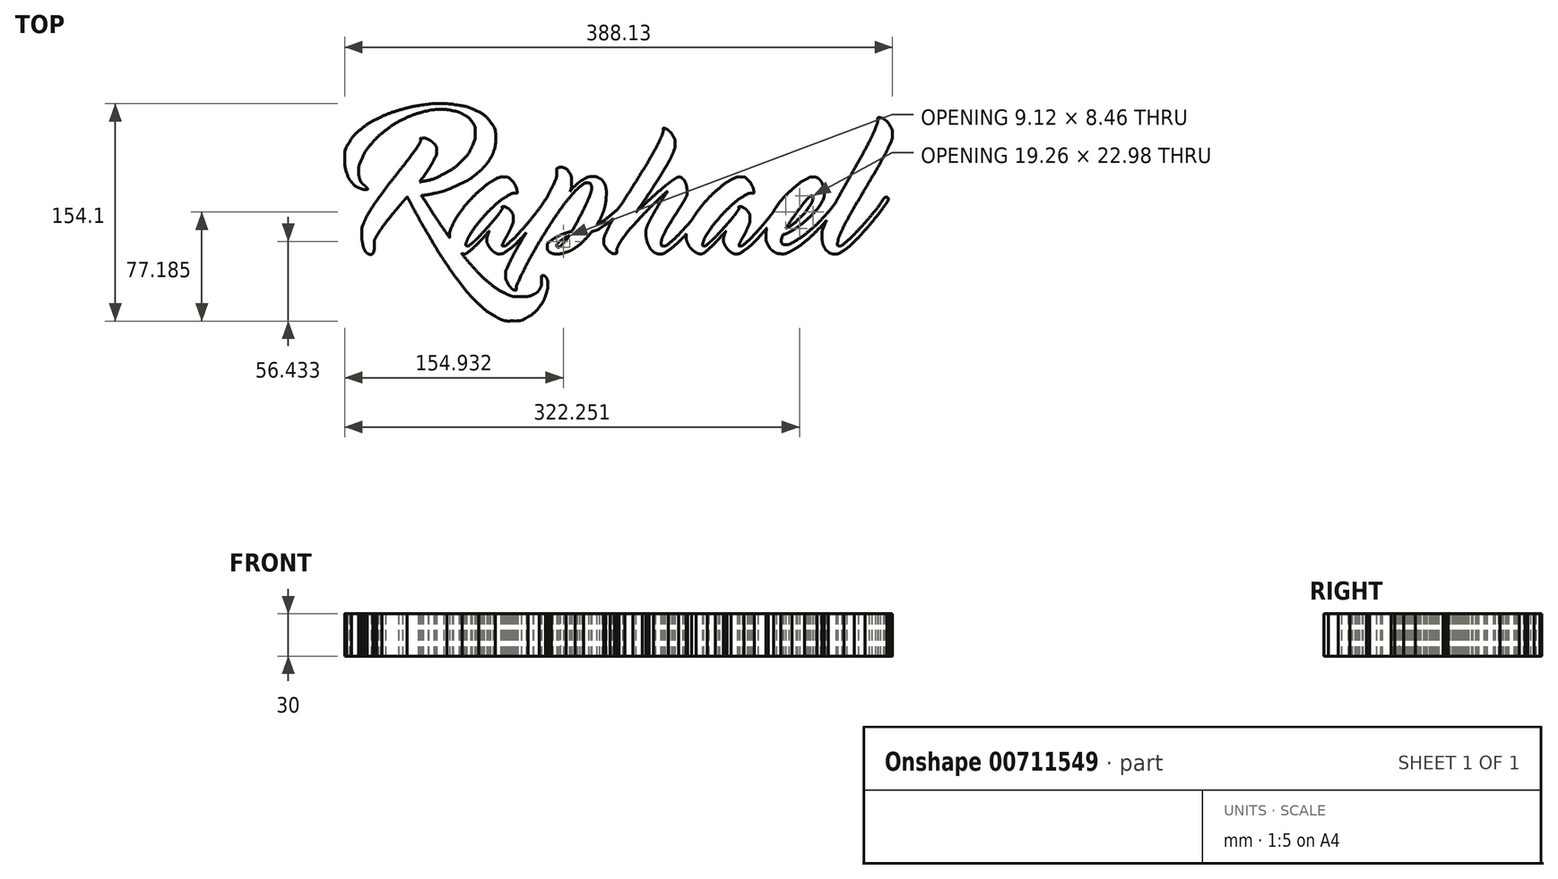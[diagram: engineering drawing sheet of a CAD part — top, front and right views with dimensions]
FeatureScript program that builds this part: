
annotation { "Feature Type Name" : "Feature", "Feature Type Description" : "" }
export const myFeature = defineFeature(function(context is Context, id is Id, definition is map)
    precondition{}
    {
        {
            var Q0;
            Q0=qCreatedBy(makeId("Top.planeOp"), FACE);
            var sketch = newSketch(context, id + "F0", { "sketchPlane" : qUnion([Q0])});
            skFitSpline(sketch, "E0", {"points": [v(158.08, -13.07) * mm, v(159.58, -9.83) * mm, v(161.51, -6.1) * mm, v(163.88, -1.91) * mm]});
            skFitSpline(sketch, "E1", {"points": [v(163.88, -1.91) * mm, v(166.25, 2.28) * mm, v(168.77, 6.64) * mm, v(171.43, 11.16) * mm]});
            skFitSpline(sketch, "E2", {"points": [v(171.43, 11.16) * mm, v(174.1, 15.68) * mm, v(176.77, 20.22) * mm, v(179.47, 24.78) * mm]});
            skFitSpline(sketch, "E3", {"points": [v(179.47, 24.78) * mm, v(182.17, 29.33) * mm, v(184.6, 33.56) * mm, v(186.77, 37.47) * mm]});
            skFitSpline(sketch, "E4", {"points": [v(186.77, 37.47) * mm, v(188.93, 41.37) * mm, v(190.68, 44.8) * mm, v(192.02, 47.75) * mm]});
            skFitSpline(sketch, "E5", {"points": [v(192.02, 47.75) * mm, v(193.35, 50.7) * mm, v(194.02, 52.87) * mm, v(194.02, 54.26) * mm, v(194.02, 57.03) * mm, v(193.48, 59.34) * mm, v(192.4, 61.2) * mm]});
            skFitSpline(sketch, "E6", {"points": [v(192.4, 61.2) * mm, v(191.31, 63.06) * mm, v(190.12, 64.48) * mm, v(188.82, 65.47) * mm]});
            skFitSpline(sketch, "E7", {"points": [v(188.82, 65.47) * mm, v(187.53, 66.45) * mm, v(186.33, 66.98) * mm, v(185.25, 67.06) * mm]});
            skFitSpline(sketch, "E8", {"points": [v(185.25, 67.06) * mm, v(184.17, 67.13) * mm, v(183.63, 66.76) * mm, v(183.63, 65.96) * mm, v(183.63, 64.5) * mm, v(183.06, 62.37) * mm, v(181.93, 59.56) * mm]});
            skFitSpline(sketch, "E9", {"points": [v(181.93, 59.56) * mm, v(180.8, 56.75) * mm, v(179.3, 53.53) * mm, v(177.45, 49.88) * mm]});
            skFitSpline(sketch, "E10", {"points": [v(177.45, 49.88) * mm, v(175.59, 46.23) * mm, v(173.47, 42.28) * mm, v(171.1, 38.01) * mm]});
            skFitSpline(sketch, "E11", {"points": [v(171.1, 38.01) * mm, v(168.73, 33.75) * mm, v(166.3, 29.43) * mm, v(163.83, 25.05) * mm]});
            skFitSpline(sketch, "E12", {"points": [v(163.83, 25.05) * mm, v(161.35, 20.67) * mm, v(158.92, 16.35) * mm, v(156.56, 12.09) * mm]});
            skFitSpline(sketch, "E13", {"points": [v(156.56, 12.09) * mm, v(155.6, 10.38) * mm, v(154.7, 8.73) * mm, v(153.84, 7.12) * mm]});
            skFitSpline(sketch, "E14", {"points": [v(153.84, 7.12) * mm, v(151.66, 4) * mm, v(149.13, 0.84) * mm, v(146.22, -2.35) * mm]});
            skFitSpline(sketch, "E15", {"points": [v(146.22, -2.35) * mm, v(142.8, -6.1) * mm, v(139.3, -9.5) * mm, v(135.77, -12.53) * mm]});
            skFitSpline(sketch, "E16", {"points": [v(135.77, -12.53) * mm, v(132.23, -15.55) * mm, v(128.9, -18.03) * mm, v(125.76, -19.96) * mm]});
            skFitSpline(sketch, "E17", {"points": [v(125.76, -19.96) * mm, v(122.63, -21.9) * mm, v(120.15, -22.86) * mm, v(118.32, -22.86) * mm, v(116.86, -22.86) * mm, v(115.97, -22.5) * mm, v(115.64, -21.77) * mm]});
            skFitSpline(sketch, "E18", {"points": [v(115.64, -21.77) * mm, v(115.31, -21.04) * mm, v(115.22, -20.2) * mm, v(115.37, -19.25) * mm]});
            skFitSpline(sketch, "E19", {"points": [v(115.37, -19.25) * mm, v(115.59, -18.16) * mm, v(116.03, -16.92) * mm, v(116.68, -15.53) * mm]});
            skFitSpline(sketch, "E20", {"points": [v(116.68, -15.53) * mm, v(117.63, -15.53) * mm, v(119, -15.08) * mm, v(120.78, -14.17) * mm]});
            skFitSpline(sketch, "E21", {"points": [v(120.78, -14.17) * mm, v(122.57, -13.25) * mm, v(124.54, -12.03) * mm, v(126.7, -10.5) * mm]});
            skFitSpline(sketch, "E22", {"points": [v(126.7, -10.5) * mm, v(128.84, -8.97) * mm, v(131.03, -7.22) * mm, v(133.25, -5.25) * mm]});
            skFitSpline(sketch, "E23", {"points": [v(133.25, -5.25) * mm, v(135.48, -3.28) * mm, v(137.5, -1.26) * mm, v(139.33, 0.82) * mm]});
            skFitSpline(sketch, "E24", {"points": [v(139.33, 0.82) * mm, v(141.15, 2.9) * mm, v(142.65, 4.98) * mm, v(143.81, 7.06) * mm]});
            skFitSpline(sketch, "E25", {"points": [v(143.81, 7.06) * mm, v(144.98, 9.13) * mm, v(145.56, 11.05) * mm, v(145.56, 12.8) * mm, v(145.56, 15.42) * mm, v(145.29, 17.54) * mm, v(144.74, 19.14) * mm]});
            skFitSpline(sketch, "E26", {"points": [v(144.74, 19.14) * mm, v(144.2, 20.75) * mm, v(143.54, 21.99) * mm, v(142.77, 22.86) * mm]});
            skFitSpline(sketch, "E27", {"points": [v(142.77, 22.86) * mm, v(142, 23.74) * mm, v(141.19, 24.34) * mm, v(140.31, 24.67) * mm]});
            skFitSpline(sketch, "E28", {"points": [v(140.31, 24.67) * mm, v(139.44, 25) * mm, v(138.63, 25.16) * mm, v(137.9, 25.16) * mm, v(136.66, 25.16) * mm, v(134.99, 24.61) * mm, v(132.87, 23.52) * mm]});
            skFitSpline(sketch, "E29", {"points": [v(132.87, 23.52) * mm, v(130.76, 22.43) * mm, v(128.48, 20.9) * mm, v(126.04, 18.92) * mm]});
            skFitSpline(sketch, "E30", {"points": [v(126.04, 18.92) * mm, v(123.6, 16.96) * mm, v(121.1, 14.66) * mm, v(118.54, 12.03) * mm]});
            skFitSpline(sketch, "E31", {"points": [v(118.54, 12.03) * mm, v(116, 9.4) * mm, v(113.67, 6.58) * mm, v(111.6, 3.56) * mm]});
            skFitSpline(sketch, "E32", {"points": [v(111.6, 3.56) * mm, v(110.77, 2.34) * mm, v(110.01, 1.1) * mm, v(109.3, -0.15) * mm]});
            skFitSpline(sketch, "E33", {"points": [v(109.3, -0.15) * mm, v(108.71, -0.92) * mm, v(108.12, -1.69) * mm, v(107.5, -2.46) * mm]});
            skFitSpline(sketch, "E34", {"points": [v(107.5, -2.46) * mm, v(104.43, -6.29) * mm, v(101.48, -9.8) * mm, v(98.64, -12.96) * mm]});
            skFitSpline(sketch, "E35", {"points": [v(98.64, -12.96) * mm, v(95.8, -16.13) * mm, v(93.24, -18.74) * mm, v(90.98, -20.78) * mm]});
            skFitSpline(sketch, "E36", {"points": [v(90.98, -20.78) * mm, v(88.72, -22.83) * mm, v(87.15, -23.85) * mm, v(86.27, -23.85) * mm, v(85.4, -23.85) * mm, v(85.25, -23.2) * mm, v(85.84, -21.93) * mm]});
            skFitSpline(sketch, "E37", {"points": [v(85.84, -21.93) * mm, v(86.42, -20.66) * mm, v(87.26, -19.05) * mm, v(88.35, -17.12) * mm]});
            skFitSpline(sketch, "E38", {"points": [v(88.35, -17.12) * mm, v(89.45, -15.19) * mm, v(90.5, -13.07) * mm, v(91.52, -10.77) * mm]});
            skFitSpline(sketch, "E39", {"points": [v(91.52, -10.77) * mm, v(92.54, -8.48) * mm, v(93.06, -6.34) * mm, v(93.06, -4.38) * mm, v(93.06, -2.4) * mm, v(92.6, -0.8) * mm, v(91.69, 0.44) * mm]});
            skFitSpline(sketch, "E40", {"points": [v(91.69, 0.44) * mm, v(90.78, 1.68) * mm, v(89.8, 2.59) * mm, v(88.73, 3.17) * mm]});
            skFitSpline(sketch, "E41", {"points": [v(88.73, 3.17) * mm, v(87.68, 3.76) * mm, v(86.77, 4.05) * mm, v(86, 4.05) * mm, v(85.24, 4.05) * mm, v(85, 3.8) * mm, v(85.3, 3.28) * mm]});
            skFitSpline(sketch, "E42", {"points": [v(85.3, 3.28) * mm, v(85.43, 2.92) * mm, v(85.02, 2) * mm, v(84.03, 0.55) * mm]});
            skFitSpline(sketch, "E43", {"points": [v(84.03, 0.55) * mm, v(83.05, -0.91) * mm, v(81.73, -2.62) * mm, v(80.1, -4.6) * mm]});
            skFitSpline(sketch, "E44", {"points": [v(80.1, -4.6) * mm, v(78.45, -6.56) * mm, v(76.63, -8.68) * mm, v(74.62, -10.94) * mm]});
            skFitSpline(sketch, "E45", {"points": [v(74.62, -10.94) * mm, v(72.62, -13.2) * mm, v(70.69, -15.28) * mm, v(68.83, -17.17) * mm]});
            skFitSpline(sketch, "E46", {"points": [v(68.83, -17.17) * mm, v(66.97, -19.07) * mm, v(65.33, -20.64) * mm, v(63.9, -21.88) * mm]});
            skFitSpline(sketch, "E47", {"points": [v(63.9, -21.88) * mm, v(62.48, -23.12) * mm, v(61.55, -23.74) * mm, v(61.11, -23.74) * mm, v(59.8, -23.74) * mm, v(59.44, -22.82) * mm, v(60.02, -21) * mm]});
            skFitSpline(sketch, "E48", {"points": [v(60.02, -21) * mm, v(60.6, -19.17) * mm, v(61.79, -16.86) * mm, v(63.58, -14.08) * mm]});
            skFitSpline(sketch, "E49", {"points": [v(63.58, -14.08) * mm, v(65.36, -11.3) * mm, v(67.62, -8.3) * mm, v(70.36, -5.09) * mm]});
            skFitSpline(sketch, "E50", {"points": [v(70.36, -5.09) * mm, v(73.1, -1.87) * mm, v(75.94, 1.13) * mm, v(78.89, 3.9) * mm]});
            skFitSpline(sketch, "E51", {"points": [v(78.89, 3.9) * mm, v(81.85, 6.69) * mm, v(84.76, 9) * mm, v(87.64, 10.82) * mm]});
            skFitSpline(sketch, "E52", {"points": [v(87.64, 10.82) * mm, v(90.52, 12.65) * mm, v(93.02, 13.56) * mm, v(95.13, 13.56) * mm, v(95.72, 13.56) * mm, v(95.92, 14.17) * mm, v(95.74, 15.37) * mm]});
            skFitSpline(sketch, "E53", {"points": [v(95.74, 15.37) * mm, v(95.55, 16.57) * mm, v(95.08, 17.9) * mm, v(94.31, 19.36) * mm]});
            skFitSpline(sketch, "E54", {"points": [v(94.31, 19.36) * mm, v(93.55, 20.82) * mm, v(92.51, 22.15) * mm, v(91.2, 23.35) * mm]});
            skFitSpline(sketch, "E55", {"points": [v(91.2, 23.35) * mm, v(89.88, 24.56) * mm, v(88.42, 25.16) * mm, v(86.82, 25.16) * mm, v(84.78, 25.16) * mm, v(82.4, 24.43) * mm, v(79.71, 22.97) * mm]});
            skFitSpline(sketch, "E56", {"points": [v(79.71, 22.97) * mm, v(77.01, 21.51) * mm, v(74.22, 19.58) * mm, v(71.34, 17.17) * mm]});
            skFitSpline(sketch, "E57", {"points": [v(71.34, 17.17) * mm, v(68.46, 14.77) * mm, v(65.62, 12.05) * mm, v(62.81, 9.02) * mm]});
            skFitSpline(sketch, "E58", {"points": [v(62.81, 9.02) * mm, v(60, 6) * mm, v(57.5, 2.93) * mm, v(55.32, -0.16) * mm]});
            skFitSpline(sketch, "E59", {"points": [v(55.32, -0.16) * mm, v(54.1, -1.9) * mm, v(53.02, -3.6) * mm, v(52.05, -5.26) * mm]});
            skFitSpline(sketch, "E60", {"points": [v(52.05, -5.26) * mm, v(49.75, -7.97) * mm, v(47.5, -10.5) * mm, v(45.3, -12.85) * mm]});
            skFitSpline(sketch, "E61", {"points": [v(45.3, -12.85) * mm, v(42.36, -16.02) * mm, v(39.71, -18.63) * mm, v(37.38, -20.67) * mm]});
            skFitSpline(sketch, "E62", {"points": [v(37.38, -20.67) * mm, v(35.04, -22.72) * mm, v(33.48, -23.74) * mm, v(32.67, -23.74) * mm, v(30.92, -23.74) * mm, v(30.12, -22.94) * mm, v(30.27, -21.33) * mm]});
            skFitSpline(sketch, "E63", {"points": [v(30.27, -21.33) * mm, v(30.41, -19.73) * mm, v(31.07, -17.7) * mm, v(32.24, -15.26) * mm]});
            skFitSpline(sketch, "E64", {"points": [v(32.24, -15.26) * mm, v(33.4, -12.82) * mm, v(34.92, -10.12) * mm, v(36.78, -7.16) * mm]});
            skFitSpline(sketch, "E65", {"points": [v(36.78, -7.16) * mm, v(38.64, -4.21) * mm, v(40.44, -1.35) * mm, v(42.2, 1.42) * mm]});
            skFitSpline(sketch, "E66", {"points": [v(42.2, 1.42) * mm, v(43.94, 4.2) * mm, v(45.45, 6.67) * mm, v(46.73, 8.86) * mm]});
            skFitSpline(sketch, "E67", {"points": [v(46.73, 8.86) * mm, v(48, 11.05) * mm, v(48.65, 12.58) * mm, v(48.65, 13.46) * mm, v(48.65, 14.77) * mm, v(48.54, 16.1) * mm, v(48.32, 17.45) * mm]});
            skFitSpline(sketch, "E68", {"points": [v(48.32, 17.45) * mm, v(48.1, 18.8) * mm, v(47.75, 20.04) * mm, v(47.28, 21.17) * mm]});
            skFitSpline(sketch, "E69", {"points": [v(47.28, 21.17) * mm, v(46.8, 22.3) * mm, v(46.18, 23.2) * mm, v(45.42, 23.9) * mm]});
            skFitSpline(sketch, "E70", {"points": [v(45.42, 23.9) * mm, v(44.65, 24.6) * mm, v(43.72, 24.94) * mm, v(42.63, 24.94) * mm, v(42.04, 24.94) * mm, v(41.17, 24.58) * mm, v(40, 23.85) * mm]});
            skFitSpline(sketch, "E71", {"points": [v(40, 23.85) * mm, v(38.84, 23.12) * mm, v(37.49, 22.17) * mm, v(35.96, 21) * mm]});
            skFitSpline(sketch, "E72", {"points": [v(35.96, 21) * mm, v(34.43, 19.84) * mm, v(32.78, 18.5) * mm, v(31.03, 17.01) * mm]});
            skFitSpline(sketch, "E73", {"points": [v(31.03, 17.01) * mm, v(29.28, 15.52) * mm, v(27.53, 14) * mm, v(25.78, 12.47) * mm]});
            skFitSpline(sketch, "E74", {"points": [v(25.78, 12.47) * mm, v(21.7, 8.82) * mm, v(17.18, 4.67) * mm, v(12.22, 0) * mm]});
            skFitSpline(sketch, "E75", {"points": [v(12.22, 0) * mm, v(17.4, 7.22) * mm, v(22.03, 14) * mm, v(26.11, 20.35) * mm]});
            skFitSpline(sketch, "E76", {"points": [v(26.11, 20.35) * mm, v(27.86, 23.04) * mm, v(29.57, 25.76) * mm, v(31.25, 28.5) * mm]});
            skFitSpline(sketch, "E77", {"points": [v(31.25, 28.5) * mm, v(32.93, 31.23) * mm, v(34.43, 33.84) * mm, v(35.74, 36.32) * mm]});
            skFitSpline(sketch, "E78", {"points": [v(35.74, 36.32) * mm, v(37.05, 38.8) * mm, v(38.1, 41.02) * mm, v(38.9, 42.99) * mm]});
            skFitSpline(sketch, "E79", {"points": [v(38.9, 42.99) * mm, v(39.71, 44.96) * mm, v(40.11, 46.53) * mm, v(40.11, 47.7) * mm, v(40.11, 49.95) * mm, v(39.67, 51.92) * mm, v(38.8, 53.6) * mm]});
            skFitSpline(sketch, "E80", {"points": [v(38.8, 53.6) * mm, v(37.92, 55.28) * mm, v(36.94, 56.6) * mm, v(35.85, 57.6) * mm]});
            skFitSpline(sketch, "E81", {"points": [v(35.85, 57.6) * mm, v(34.75, 58.58) * mm, v(33.77, 59.2) * mm, v(32.9, 59.45) * mm]});
            skFitSpline(sketch, "E82", {"points": [v(32.9, 59.45) * mm, v(32.02, 59.7) * mm, v(31.58, 59.58) * mm, v(31.58, 59.07) * mm, v(31.58, 57.54) * mm, v(30.98, 55.39) * mm, v(29.78, 52.62) * mm]});
            skFitSpline(sketch, "E83", {"points": [v(29.78, 52.62) * mm, v(28.57, 49.84) * mm, v(26.99, 46.67) * mm, v(25.02, 43.1) * mm]});
            skFitSpline(sketch, "E84", {"points": [v(25.02, 43.1) * mm, v(23.05, 39.53) * mm, v(20.8, 35.68) * mm, v(18.3, 31.56) * mm]});
            skFitSpline(sketch, "E85", {"points": [v(18.3, 31.56) * mm, v(15.77, 27.44) * mm, v(13.18, 23.26) * mm, v(10.52, 19.03) * mm]});
            skFitSpline(sketch, "E86", {"points": [v(10.52, 19.03) * mm, v(7.9, 14.88) * mm, v(5.37, 10.8) * mm, v(2.9, 6.79) * mm]});
            skFitSpline(sketch, "E87", {"points": [v(2.9, 6.79) * mm, v(0.42, 3.52) * mm, v(-2.28, 0.69) * mm, v(-5.21, -1.7) * mm]});
            skFitSpline(sketch, "E88", {"points": [v(-5.21, -1.7) * mm, v(-8.93, -4.72) * mm, v(-12.36, -7.07) * mm, v(-15.5, -8.75) * mm]});
            skFitSpline(sketch, "E89", {"points": [v(-15.5, -8.75) * mm, v(-13.98, -6.5) * mm, v(-12.77, -4.3) * mm, v(-11.87, -2.19) * mm]});
            skFitSpline(sketch, "E90", {"points": [v(-11.87, -2.19) * mm, v(-10.97, -0.07) * mm, v(-10.28, 1.95) * mm, v(-9.81, 3.88) * mm]});
            skFitSpline(sketch, "E91", {"points": [v(-9.81, 3.88) * mm, v(-9.34, 5.82) * mm, v(-9.03, 7.62) * mm, v(-8.9, 9.3) * mm]});
            skFitSpline(sketch, "E92", {"points": [v(-8.9, 9.3) * mm, v(-8.75, 10.97) * mm, v(-8.67, 12.47) * mm, v(-8.67, 13.78) * mm, v(-8.67, 15.02) * mm, v(-8.82, 16.32) * mm, v(-9.11, 17.67) * mm]});
            skFitSpline(sketch, "E93", {"points": [v(-9.11, 17.67) * mm, v(-9.4, 19.01) * mm, v(-9.92, 20.25) * mm, v(-10.64, 21.39) * mm]});
            skFitSpline(sketch, "E94", {"points": [v(-10.64, 21.39) * mm, v(-11.37, 22.52) * mm, v(-12.37, 23.45) * mm, v(-13.65, 24.18) * mm]});
            skFitSpline(sketch, "E95", {"points": [v(-13.65, 24.18) * mm, v(-14.93, 24.9) * mm, v(-16.55, 25.27) * mm, v(-18.52, 25.27) * mm, v(-20.48, 25.27) * mm, v(-22.42, 24.72) * mm, v(-24.31, 23.63) * mm]});
            skFitSpline(sketch, "E96", {"points": [v(-24.31, 23.63) * mm, v(-26.2, 22.53) * mm, v(-27.88, 21.37) * mm, v(-29.34, 20.13) * mm]});
            skFitSpline(sketch, "E97", {"points": [v(-29.34, 20.13) * mm, v(-31.1, 18.6) * mm, v(-32.73, 16.88) * mm, v(-34.26, 14.99) * mm]});
            skFitSpline(sketch, "E98", {"points": [v(-34.26, 14.99) * mm, v(-34.12, 15.35) * mm, v(-33.97, 15.79) * mm, v(-33.83, 16.3) * mm]});
            skFitSpline(sketch, "E99", {"points": [v(-33.83, 16.3) * mm, v(-33.68, 16.74) * mm, v(-33.56, 17.26) * mm, v(-33.45, 17.88) * mm]});
            skFitSpline(sketch, "E100", {"points": [v(-33.45, 17.88) * mm, v(-33.34, 18.5) * mm, v(-33.29, 19.22) * mm, v(-33.29, 20.02) * mm, v(-33.29, 23.66) * mm, v(-33.85, 26.36) * mm, v(-34.96, 28.11) * mm]});
            skFitSpline(sketch, "E101", {"points": [v(-34.96, 28.11) * mm, v(-36.08, 29.86) * mm, v(-37.3, 31) * mm, v(-38.6, 31.5) * mm]});
            skFitSpline(sketch, "E102", {"points": [v(-38.6, 31.5) * mm, v(-39.9, 32.01) * mm, v(-41.1, 32.09) * mm, v(-42.22, 31.72) * mm]});
            skFitSpline(sketch, "E103", {"points": [v(-42.22, 31.72) * mm, v(-43.33, 31.36) * mm, v(-43.9, 30.92) * mm, v(-43.9, 30.42) * mm, v(-43.9, 30.41) * mm, v(-43.9, 30.4) * mm, v(-43.9, 27.46) * mm, v(-43.9, 27.46) * mm, v(-43.9, 27.45) * mm, v(-43.9, 25.48) * mm, v(-44.8, 22.62) * mm, v(-46.58, 18.87) * mm]});
            skFitSpline(sketch, "E104", {"points": [v(-46.58, 18.87) * mm, v(-47.97, 15.94) * mm, v(-49.65, 12.7) * mm, v(-51.6, 9.2) * mm]});
            skFitSpline(sketch, "E105", {"points": [v(-51.6, 9.2) * mm, v(-51.74, 9.07) * mm, v(-51.87, 8.92) * mm, v(-52, 8.75) * mm]});
            skFitSpline(sketch, "E106", {"points": [v(-52, 8.75) * mm, v(-54.4, 5.1) * mm, v(-57.13, 1.37) * mm, v(-60.2, -2.46) * mm]});
            skFitSpline(sketch, "E107", {"points": [v(-60.2, -2.46) * mm, v(-63.26, -6.29) * mm, v(-66.21, -9.8) * mm, v(-69.06, -12.96) * mm]});
            skFitSpline(sketch, "E108", {"points": [v(-69.06, -12.96) * mm, v(-71.9, -16.13) * mm, v(-74.45, -18.74) * mm, v(-76.71, -20.78) * mm]});
            skFitSpline(sketch, "E109", {"points": [v(-76.71, -20.78) * mm, v(-78.97, -22.83) * mm, v(-80.54, -23.85) * mm, v(-81.42, -23.85) * mm, v(-82.3, -23.85) * mm, v(-82.44, -23.2) * mm, v(-81.85, -21.93) * mm]});
            skFitSpline(sketch, "E110", {"points": [v(-81.85, -21.93) * mm, v(-81.27, -20.66) * mm, v(-80.43, -19.05) * mm, v(-79.34, -17.12) * mm]});
            skFitSpline(sketch, "E111", {"points": [v(-79.34, -17.12) * mm, v(-78.24, -15.19) * mm, v(-77.19, -13.07) * mm, v(-76.17, -10.77) * mm]});
            skFitSpline(sketch, "E112", {"points": [v(-76.17, -10.77) * mm, v(-75.15, -8.48) * mm, v(-74.63, -6.34) * mm, v(-74.63, -4.38) * mm, v(-74.63, -2.4) * mm, v(-75.1, -0.8) * mm, v(-76, 0.44) * mm]});
            skFitSpline(sketch, "E113", {"points": [v(-76, 0.44) * mm, v(-76.91, 1.68) * mm, v(-77.9, 2.59) * mm, v(-78.96, 3.17) * mm]});
            skFitSpline(sketch, "E114", {"points": [v(-78.96, 3.17) * mm, v(-80.01, 3.76) * mm, v(-80.92, 4.05) * mm, v(-81.69, 4.05) * mm, v(-82.46, 4.05) * mm, v(-82.7, 3.8) * mm, v(-82.4, 3.28) * mm]});
            skFitSpline(sketch, "E115", {"points": [v(-82.4, 3.28) * mm, v(-82.26, 2.92) * mm, v(-82.67, 2) * mm, v(-83.66, 0.55) * mm]});
            skFitSpline(sketch, "E116", {"points": [v(-83.66, 0.55) * mm, v(-84.64, -0.91) * mm, v(-85.96, -2.62) * mm, v(-87.6, -4.6) * mm]});
            skFitSpline(sketch, "E117", {"points": [v(-87.6, -4.6) * mm, v(-89.24, -6.56) * mm, v(-91.06, -8.68) * mm, v(-93.07, -10.94) * mm]});
            skFitSpline(sketch, "E118", {"points": [v(-93.07, -10.94) * mm, v(-95.07, -13.2) * mm, v(-97, -15.28) * mm, v(-98.86, -17.17) * mm]});
            skFitSpline(sketch, "E119", {"points": [v(-98.86, -17.17) * mm, v(-100.72, -19.07) * mm, v(-102.36, -20.64) * mm, v(-103.79, -21.88) * mm]});
            skFitSpline(sketch, "E120", {"points": [v(-103.79, -21.88) * mm, v(-105.2, -23.12) * mm, v(-106.14, -23.74) * mm, v(-106.58, -23.74) * mm, v(-107.89, -23.74) * mm, v(-108.25, -22.82) * mm, v(-107.67, -21) * mm]});
            skFitSpline(sketch, "E121", {"points": [v(-107.67, -21) * mm, v(-107.09, -19.17) * mm, v(-105.9, -16.86) * mm, v(-104.11, -14.08) * mm]});
            skFitSpline(sketch, "E122", {"points": [v(-104.11, -14.08) * mm, v(-102.33, -11.3) * mm, v(-100.07, -8.3) * mm, v(-97.33, -5.09) * mm]});
            skFitSpline(sketch, "E123", {"points": [v(-97.33, -5.09) * mm, v(-94.6, -1.87) * mm, v(-91.75, 1.13) * mm, v(-88.8, 3.9) * mm]});
            skFitSpline(sketch, "E124", {"points": [v(-88.8, 3.9) * mm, v(-85.85, 6.69) * mm, v(-82.93, 9) * mm, v(-80.05, 10.82) * mm]});
            skFitSpline(sketch, "E125", {"points": [v(-80.05, 10.82) * mm, v(-77.17, 12.65) * mm, v(-74.67, 13.56) * mm, v(-72.56, 13.56) * mm, v(-71.97, 13.56) * mm, v(-71.77, 14.17) * mm, v(-71.95, 15.37) * mm]});
            skFitSpline(sketch, "E126", {"points": [v(-71.95, 15.37) * mm, v(-72.14, 16.57) * mm, v(-72.61, 17.9) * mm, v(-73.38, 19.36) * mm]});
            skFitSpline(sketch, "E127", {"points": [v(-73.38, 19.36) * mm, v(-74.14, 20.82) * mm, v(-75.18, 22.15) * mm, v(-76.5, 23.35) * mm]});
            skFitSpline(sketch, "E128", {"points": [v(-76.5, 23.35) * mm, v(-77.8, 24.56) * mm, v(-79.27, 25.16) * mm, v(-80.87, 25.16) * mm, v(-82.91, 25.16) * mm, v(-85.28, 24.43) * mm, v(-87.98, 22.97) * mm]});
            skFitSpline(sketch, "E129", {"points": [v(-87.98, 22.97) * mm, v(-90.68, 21.51) * mm, v(-93.47, 19.58) * mm, v(-96.35, 17.17) * mm]});
            skFitSpline(sketch, "E130", {"points": [v(-96.35, 17.17) * mm, v(-99.23, 14.77) * mm, v(-102.07, 12.05) * mm, v(-104.88, 9.02) * mm]});
            skFitSpline(sketch, "E131", {"points": [v(-104.88, 9.02) * mm, v(-107.69, 6) * mm, v(-110.19, 2.93) * mm, v(-112.37, -0.16) * mm]});
            skFitSpline(sketch, "E132", {"points": [v(-112.37, -0.16) * mm, v(-114.56, -3.26) * mm, v(-116.33, -6.25) * mm, v(-117.68, -9.13) * mm]});
            skFitSpline(sketch, "E133", {"points": [v(-117.68, -9.13) * mm, v(-119.03, -12.02) * mm, v(-119.7, -14.51) * mm, v(-119.7, -16.63) * mm, v(-119.7, -17.1) * mm, v(-119.68, -17.57) * mm, v(-119.64, -18.02) * mm]});
            skFitSpline(sketch, "E134", {"points": [v(-119.64, -18.02) * mm, v(-120.18, -17.26) * mm, v(-120.75, -16.5) * mm, v(-121.28, -15.75) * mm]});
            skFitSpline(sketch, "E135", {"points": [v(-121.28, -15.75) * mm, v(-124.2, -11.6) * mm, v(-126.86, -7.7) * mm, v(-129.26, -4.05) * mm]});
            skFitSpline(sketch, "E136", {"points": [v(-129.26, -4.05) * mm, v(-131.67, -0.4) * mm, v(-133.77, 2.83) * mm, v(-135.55, 5.63) * mm]});
            skFitSpline(sketch, "E137", {"points": [v(-135.55, 5.63) * mm, v(-137.34, 8.44) * mm, v(-138.74, 10.54) * mm, v(-139.76, 11.92) * mm]});
            skFitSpline(sketch, "E138", {"points": [v(-139.76, 11.92) * mm, v(-136.7, 12.29) * mm, v(-133.31, 12.87) * mm, v(-129.6, 13.67) * mm]});
            skFitSpline(sketch, "E139", {"points": [v(-129.6, 13.67) * mm, v(-125.88, 14.47) * mm, v(-122.27, 15.6) * mm, v(-118.77, 17.06) * mm, v(-118.76, 17.06) * mm, v(-118.76, 17.07) * mm, v(-112.75, 19.8) * mm, v(-112.74, 19.8) * mm, v(-112.74, 19.8) * mm, v(-108, 22.06) * mm, v(-103.74, 24.76) * mm, v(-99.95, 27.9) * mm]});
            skFitSpline(sketch, "E140", {"points": [v(-99.95, 27.9) * mm, v(-98.34, 29.2) * mm, v(-96.77, 30.7) * mm, v(-95.24, 32.38) * mm]});
            skFitSpline(sketch, "E141", {"points": [v(-95.24, 32.38) * mm, v(-93.71, 34.06) * mm, v(-92.34, 35.86) * mm, v(-91.14, 37.8) * mm]});
            skFitSpline(sketch, "E142", {"points": [v(-91.14, 37.8) * mm, v(-89.94, 39.73) * mm, v(-88.97, 41.82) * mm, v(-88.24, 44.08) * mm]});
            skFitSpline(sketch, "E143", {"points": [v(-88.24, 44.08) * mm, v(-87.51, 46.34) * mm, v(-87.15, 48.75) * mm, v(-87.15, 51.3) * mm, v(-87.15, 56.4) * mm, v(-88.4, 60.64) * mm, v(-90.92, 64) * mm]});
            skFitSpline(sketch, "E144", {"points": [v(-90.92, 64) * mm, v(-93.44, 67.35) * mm, v(-96.61, 69.97) * mm, v(-100.44, 71.87) * mm]});
            skFitSpline(sketch, "E145", {"points": [v(-100.44, 71.87) * mm, v(-104.27, 73.76) * mm, v(-108.5, 75.1) * mm, v(-113.13, 75.86) * mm]});
            skFitSpline(sketch, "E146", {"points": [v(-113.13, 75.86) * mm, v(-117.76, 76.63) * mm, v(-122.2, 77) * mm, v(-126.42, 77) * mm, v(-130.87, 77) * mm, v(-135.63, 76.6) * mm, v(-140.7, 75.8) * mm]});
            skFitSpline(sketch, "E147", {"points": [v(-140.7, 75.8) * mm, v(-145.76, 75) * mm, v(-150.8, 73.84) * mm, v(-155.79, 72.3) * mm]});
            skFitSpline(sketch, "E148", {"points": [v(-155.79, 72.3) * mm, v(-160.79, 70.77) * mm, v(-165.58, 68.9) * mm, v(-170.17, 66.67) * mm]});
            skFitSpline(sketch, "E149", {"points": [v(-170.17, 66.67) * mm, v(-174.77, 64.45) * mm, v(-178.83, 61.9) * mm, v(-182.37, 59.02) * mm]});
            skFitSpline(sketch, "E150", {"points": [v(-182.37, 59.02) * mm, v(-185.9, 56.13) * mm, v(-188.73, 52.94) * mm, v(-190.85, 49.44) * mm]});
            skFitSpline(sketch, "E151", {"points": [v(-190.85, 49.44) * mm, v(-192.96, 45.94) * mm, v(-194.02, 42.19) * mm, v(-194.02, 38.18) * mm, v(-194.02, 34.31) * mm, v(-193.56, 31) * mm, v(-192.65, 28.22) * mm]});
            skFitSpline(sketch, "E152", {"points": [v(-192.65, 28.22) * mm, v(-191.74, 25.45) * mm, v(-190.56, 23.17) * mm, v(-189.1, 21.39) * mm]});
            skFitSpline(sketch, "E153", {"points": [v(-189.1, 21.39) * mm, v(-187.64, 19.6) * mm, v(-185.98, 18.29) * mm, v(-184.12, 17.45) * mm]});
            skFitSpline(sketch, "E154", {"points": [v(-184.12, 17.45) * mm, v(-182.26, 16.6) * mm, v(-180.38, 16.2) * mm, v(-178.49, 16.2) * mm, v(-177.9, 16.2) * mm, v(-177.7, 16.35) * mm, v(-177.89, 16.68) * mm]});
            skFitSpline(sketch, "E155", {"points": [v(-177.89, 16.68) * mm, v(-178.07, 17.01) * mm, v(-178.34, 17.4) * mm, v(-178.7, 17.83) * mm]});
            skFitSpline(sketch, "E156", {"points": [v(-178.7, 17.83) * mm, v(-179.14, 18.27) * mm, v(-179.73, 18.81) * mm, v(-180.46, 19.47) * mm]});
            skFitSpline(sketch, "E157", {"points": [v(-180.46, 19.47) * mm, v(-180.82, 19.7) * mm, v(-181.16, 19.95) * mm, v(-181.47, 20.26) * mm]});
            skFitSpline(sketch, "E158", {"points": [v(-181.47, 20.26) * mm, v(-181.78, 20.57) * mm, v(-182.06, 20.93) * mm, v(-182.32, 21.33) * mm]});
            skFitSpline(sketch, "E159", {"points": [v(-182.32, 21.33) * mm, v(-182.75, 21.99) * mm, v(-183.16, 22.88) * mm, v(-183.52, 24.01) * mm]});
            skFitSpline(sketch, "E160", {"points": [v(-183.52, 24.01) * mm, v(-183.89, 25.14) * mm, v(-184.07, 26.58) * mm, v(-184.07, 28.33) * mm, v(-184.07, 31.61) * mm, v(-183.26, 35) * mm, v(-181.66, 38.5) * mm]});
            skFitSpline(sketch, "E161", {"points": [v(-181.66, 38.5) * mm, v(-180.06, 42) * mm, v(-177.85, 45.4) * mm, v(-175.04, 48.68) * mm]});
            skFitSpline(sketch, "E162", {"points": [v(-175.04, 48.68) * mm, v(-172.24, 51.96) * mm, v(-168.93, 55.08) * mm, v(-165.14, 58.03) * mm]});
            skFitSpline(sketch, "E163", {"points": [v(-165.14, 58.03) * mm, v(-161.35, 60.98) * mm, v(-157.27, 63.55) * mm, v(-152.9, 65.74) * mm]});
            skFitSpline(sketch, "E164", {"points": [v(-152.9, 65.74) * mm, v(-148.52, 67.93) * mm, v(-143.96, 69.66) * mm, v(-139.22, 70.94) * mm]});
            skFitSpline(sketch, "E165", {"points": [v(-139.22, 70.94) * mm, v(-134.48, 72.21) * mm, v(-129.74, 72.85) * mm, v(-125, 72.85) * mm, v(-122.52, 72.85) * mm, v(-119.91, 72.56) * mm, v(-117.18, 71.98) * mm]});
            skFitSpline(sketch, "E166", {"points": [v(-117.18, 71.98) * mm, v(-114.44, 71.4) * mm, v(-111.9, 70.45) * mm, v(-109.57, 69.13) * mm]});
            skFitSpline(sketch, "E167", {"points": [v(-109.57, 69.13) * mm, v(-107.24, 67.82) * mm, v(-105.3, 66.13) * mm, v(-103.78, 64.05) * mm]});
            skFitSpline(sketch, "E168", {"points": [v(-103.78, 64.05) * mm, v(-102.24, 61.97) * mm, v(-101.48, 59.4) * mm, v(-101.48, 56.34) * mm, v(-101.48, 53.27) * mm, v(-102.32, 49.95) * mm, v(-104, 46.38) * mm]});
            skFitSpline(sketch, "E169", {"points": [v(-104, 46.38) * mm, v(-105.67, 42.8) * mm, v(-108.19, 39.38) * mm, v(-111.54, 36.1) * mm]});
            skFitSpline(sketch, "E170", {"points": [v(-111.54, 36.1) * mm, v(-114.9, 32.82) * mm, v(-119.04, 29.86) * mm, v(-123.96, 27.24) * mm]});
            skFitSpline(sketch, "E171", {"points": [v(-123.96, 27.24) * mm, v(-128.88, 24.61) * mm, v(-134.59, 22.72) * mm, v(-141.08, 21.55) * mm]});
            skFitSpline(sketch, "E172", {"points": [v(-141.08, 21.55) * mm, v(-138.82, 24.47) * mm, v(-136.77, 27.3) * mm, v(-134.95, 30.08) * mm]});
            skFitSpline(sketch, "E173", {"points": [v(-134.95, 30.08) * mm, v(-133.42, 32.41) * mm, v(-132.02, 34.86) * mm, v(-130.74, 37.41) * mm]});
            skFitSpline(sketch, "E174", {"points": [v(-130.74, 37.41) * mm, v(-129.46, 39.96) * mm, v(-128.83, 42.11) * mm, v(-128.83, 43.86) * mm, v(-128.83, 45.62) * mm, v(-129.43, 47.15) * mm, v(-130.63, 48.46) * mm]});
            skFitSpline(sketch, "E175", {"points": [v(-130.63, 48.46) * mm, v(-131.83, 49.77) * mm, v(-133.15, 50.8) * mm, v(-134.57, 51.52) * mm]});
            skFitSpline(sketch, "E176", {"points": [v(-134.57, 51.52) * mm, v(-136, 52.25) * mm, v(-137.29, 52.65) * mm, v(-138.45, 52.73) * mm]});
            skFitSpline(sketch, "E177", {"points": [v(-138.45, 52.73) * mm, v(-139.62, 52.8) * mm, v(-140.2, 52.47) * mm, v(-140.2, 51.74) * mm, v(-140.2, 50.8) * mm, v(-140.8, 49.33) * mm, v(-142, 47.37) * mm]});
            skFitSpline(sketch, "E178", {"points": [v(-142, 47.37) * mm, v(-143.2, 45.4) * mm, v(-144.8, 43.1) * mm, v(-146.76, 40.47) * mm]});
            skFitSpline(sketch, "E179", {"points": [v(-146.76, 40.47) * mm, v(-148.73, 37.85) * mm, v(-150.96, 34.97) * mm, v(-153.44, 31.83) * mm]});
            skFitSpline(sketch, "E180", {"points": [v(-153.44, 31.83) * mm, v(-155.92, 28.7) * mm, v(-158.47, 25.45) * mm, v(-161.1, 22.1) * mm]});
            skFitSpline(sketch, "E181", {"points": [v(-161.1, 22.1) * mm, v(-163.72, 18.74) * mm, v(-166.27, 15.37) * mm, v(-168.75, 11.98) * mm]});
            skFitSpline(sketch, "E182", {"points": [v(-168.75, 11.98) * mm, v(-171.23, 8.59) * mm, v(-173.46, 5.32) * mm, v(-175.42, 2.19) * mm]});
            skFitSpline(sketch, "E183", {"points": [v(-175.42, 2.19) * mm, v(-177.4, -0.95) * mm, v(-178.98, -3.88) * mm, v(-180.18, -6.62) * mm]});
            skFitSpline(sketch, "E184", {"points": [v(-180.18, -6.62) * mm, v(-181.39, -9.35) * mm, v(-181.99, -11.7) * mm, v(-181.99, -13.67) * mm, v(-181.99, -16.74) * mm, v(-181.82, -19.29) * mm, v(-181.5, -21.33) * mm]});
            skFitSpline(sketch, "E185", {"points": [v(-181.5, -21.33) * mm, v(-181.17, -23.37) * mm, v(-180.71, -25.01) * mm, v(-180.13, -26.25) * mm]});
            skFitSpline(sketch, "E186", {"points": [v(-180.13, -26.25) * mm, v(-179.55, -27.5) * mm, v(-178.87, -28.39) * mm, v(-178.1, -28.93) * mm]});
            skFitSpline(sketch, "E187", {"points": [v(-178.1, -28.93) * mm, v(-177.34, -29.48) * mm, v(-176.52, -29.75) * mm, v(-175.64, -29.75) * mm, v(-174.84, -29.75) * mm, v(-174.26, -29.42) * mm, v(-173.9, -28.77) * mm]});
            skFitSpline(sketch, "E188", {"points": [v(-173.9, -28.77) * mm, v(-173.53, -28.11) * mm, v(-173.3, -27.33) * mm, v(-173.18, -26.42) * mm]});
            skFitSpline(sketch, "E189", {"points": [v(-173.18, -26.42) * mm, v(-173.07, -25.5) * mm, v(-173.04, -24.6) * mm, v(-173.07, -23.68) * mm]});
            skFitSpline(sketch, "E190", {"points": [v(-173.07, -23.68) * mm, v(-173.11, -22.77) * mm, v(-173.13, -22.02) * mm, v(-173.13, -21.44) * mm, v(-173.13, -20.42) * mm, v(-172.62, -19) * mm, v(-171.6, -17.17) * mm]});
            skFitSpline(sketch, "E191", {"points": [v(-171.6, -17.17) * mm, v(-170.58, -15.35) * mm, v(-169.3, -13.34) * mm, v(-167.77, -11.16) * mm]});
            skFitSpline(sketch, "E192", {"points": [v(-167.77, -11.16) * mm, v(-166.24, -8.97) * mm, v(-164.54, -6.7) * mm, v(-162.68, -4.38) * mm]});
            skFitSpline(sketch, "E193", {"points": [v(-162.68, -4.38) * mm, v(-160.82, -2.04) * mm, v(-159.02, 0.16) * mm, v(-157.27, 2.24) * mm]});
            skFitSpline(sketch, "E194", {"points": [v(-157.27, 2.24) * mm, v(-155.52, 4.32) * mm, v(-153.97, 6.14) * mm, v(-152.62, 7.71) * mm]});
            skFitSpline(sketch, "E195", {"points": [v(-152.62, 7.71) * mm, v(-151.27, 9.28) * mm, v(-150.34, 10.4) * mm, v(-149.83, 11.05) * mm]});
            skFitSpline(sketch, "E196", {"points": [v(-149.83, 11.05) * mm, v(-149.03, 9.59) * mm, v(-147.75, 7.22) * mm, v(-146, 3.94) * mm]});
            skFitSpline(sketch, "E197", {"points": [v(-146, 3.94) * mm, v(-144.25, 0.66) * mm, v(-142.13, -3.17) * mm, v(-139.65, -7.55) * mm]});
            skFitSpline(sketch, "E198", {"points": [v(-139.65, -7.55) * mm, v(-137.18, -11.92) * mm, v(-134.4, -16.68) * mm, v(-131.34, -21.82) * mm]});
            skFitSpline(sketch, "E199", {"points": [v(-131.34, -21.82) * mm, v(-128.28, -26.96) * mm, v(-125.02, -32.1) * mm, v(-121.55, -37.25) * mm]});
            skFitSpline(sketch, "E200", {"points": [v(-121.55, -37.25) * mm, v(-118.09, -42.39) * mm, v(-114.46, -47.37) * mm, v(-110.67, -52.18) * mm]});
            skFitSpline(sketch, "E201", {"points": [v(-110.67, -52.18) * mm, v(-106.88, -57) * mm, v(-103.03, -61.22) * mm, v(-99.13, -64.87) * mm]});
            skFitSpline(sketch, "E202", {"points": [v(-99.13, -64.87) * mm, v(-95.23, -68.51) * mm, v(-91.32, -71.45) * mm, v(-87.42, -73.67) * mm]});
            skFitSpline(sketch, "E203", {"points": [v(-87.42, -73.67) * mm, v(-83.52, -75.9) * mm, v(-79.71, -77) * mm, v(-76, -77) * mm, v(-71.4, -77) * mm, v(-67.48, -76.04) * mm, v(-64.23, -74.11) * mm]});
            skFitSpline(sketch, "E204", {"points": [v(-64.23, -74.11) * mm, v(-60.99, -72.18) * mm, v(-58.32, -69.86) * mm, v(-56.25, -67.16) * mm]});
            skFitSpline(sketch, "E205", {"points": [v(-56.25, -67.16) * mm, v(-54.17, -64.46) * mm, v(-52.64, -61.66) * mm, v(-51.65, -58.74) * mm]});
            skFitSpline(sketch, "E206", {"points": [v(-51.65, -58.74) * mm, v(-50.67, -55.82) * mm, v(-50.18, -53.38) * mm, v(-50.18, -51.41) * mm, v(-50.18, -49.44) * mm, v(-50.4, -48) * mm, v(-50.83, -47.1) * mm]});
            skFitSpline(sketch, "E207", {"points": [v(-50.83, -47.1) * mm, v(-51.27, -46.18) * mm, v(-51.78, -45.54) * mm, v(-52.36, -45.18) * mm]});
            skFitSpline(sketch, "E208", {"points": [v(-52.36, -45.18) * mm, v(-53.02, -44.81) * mm, v(-53.75, -44.7) * mm, v(-54.55, -44.85) * mm]});
            skFitSpline(sketch, "E209", {"points": [v(-54.55, -44.85) * mm, v(-54.55, -46.38) * mm, v(-54.57, -48.02) * mm, v(-54.6, -49.77) * mm]});
            skFitSpline(sketch, "E210", {"points": [v(-54.6, -49.77) * mm, v(-54.64, -51.52) * mm, v(-55.14, -53.14) * mm, v(-56.08, -54.64) * mm]});
            skFitSpline(sketch, "E211", {"points": [v(-56.08, -54.64) * mm, v(-57.03, -56.13) * mm, v(-58.6, -57.37) * mm, v(-60.79, -58.36) * mm]});
            skFitSpline(sketch, "E212", {"points": [v(-60.79, -58.36) * mm, v(-62.97, -59.34) * mm, v(-66.22, -59.84) * mm, v(-70.52, -59.84) * mm, v(-73.8, -59.84) * mm, v(-77.21, -58.96) * mm, v(-80.75, -57.2) * mm]});
            skFitSpline(sketch, "E213", {"points": [v(-80.75, -57.2) * mm, v(-84.29, -55.46) * mm, v(-87.82, -53.12) * mm, v(-91.36, -50.2) * mm]});
            skFitSpline(sketch, "E214", {"points": [v(-91.36, -50.2) * mm, v(-94.9, -47.3) * mm, v(-98.41, -43.92) * mm, v(-101.92, -40.1) * mm]});
            skFitSpline(sketch, "E215", {"points": [v(-101.92, -40.1) * mm, v(-105.15, -36.56) * mm, v(-108.26, -32.88) * mm, v(-111.27, -29.1) * mm]});
            skFitSpline(sketch, "E216", {"points": [v(-111.27, -29.1) * mm, v(-110.63, -29.3) * mm, v(-110.01, -29.42) * mm, v(-109.42, -29.42) * mm, v(-108.4, -29.42) * mm, v(-106.9, -28.59) * mm, v(-104.93, -26.91) * mm]});
            skFitSpline(sketch, "E217", {"points": [v(-104.93, -26.91) * mm, v(-102.97, -25.23) * mm, v(-101, -23.37) * mm, v(-99.03, -21.33) * mm]});
            skFitSpline(sketch, "E218", {"points": [v(-99.03, -21.33) * mm, v(-96.7, -18.92) * mm, v(-94.22, -16.23) * mm, v(-91.59, -13.24) * mm]});
            skFitSpline(sketch, "E219", {"points": [v(-91.59, -13.24) * mm, v(-91.96, -14.04) * mm, v(-92.28, -14.84) * mm, v(-92.57, -15.64) * mm]});
            skFitSpline(sketch, "E220", {"points": [v(-92.57, -15.64) * mm, v(-92.8, -16.3) * mm, v(-93, -17) * mm, v(-93.18, -17.78) * mm]});
            skFitSpline(sketch, "E221", {"points": [v(-93.18, -17.78) * mm, v(-93.36, -18.54) * mm, v(-93.45, -19.25) * mm, v(-93.45, -19.9) * mm, v(-93.45, -20.56) * mm, v(-93.2, -21.44) * mm, v(-92.68, -22.53) * mm]});
            skFitSpline(sketch, "E222", {"points": [v(-92.68, -22.53) * mm, v(-92.17, -23.63) * mm, v(-91.52, -24.69) * mm, v(-90.71, -25.7) * mm]});
            skFitSpline(sketch, "E223", {"points": [v(-90.71, -25.7) * mm, v(-89.91, -26.73) * mm, v(-88.96, -27.6) * mm, v(-87.87, -28.33) * mm]});
            skFitSpline(sketch, "E224", {"points": [v(-87.87, -28.33) * mm, v(-86.78, -29.06) * mm, v(-85.68, -29.42) * mm, v(-84.59, -29.42) * mm, v(-82.91, -29.42) * mm, v(-80.94, -28.64) * mm, v(-78.68, -27.07) * mm]});
            skFitSpline(sketch, "E225", {"points": [v(-78.68, -27.07) * mm, v(-76.42, -25.5) * mm, v(-74.05, -23.47) * mm, v(-71.57, -21) * mm]});
            skFitSpline(sketch, "E226", {"points": [v(-71.57, -21) * mm, v(-69.55, -18.97) * mm, v(-67.52, -16.79) * mm, v(-65.5, -14.45) * mm]});
            skFitSpline(sketch, "E227", {"points": [v(-65.5, -14.45) * mm, v(-67.3, -17.5) * mm, v(-69.04, -20.47) * mm, v(-70.7, -23.35) * mm]});
            skFitSpline(sketch, "E228", {"points": [v(-70.7, -23.35) * mm, v(-73.4, -28.06) * mm, v(-75.64, -32.29) * mm, v(-77.42, -36.04) * mm]});
            skFitSpline(sketch, "E229", {"points": [v(-77.42, -36.04) * mm, v(-79.21, -39.8) * mm, v(-80.1, -42.62) * mm, v(-80.1, -44.52) * mm, v(-80.1, -46.27) * mm, v(-79.7, -47.95) * mm, v(-78.9, -49.55) * mm]});
            skFitSpline(sketch, "E230", {"points": [v(-78.9, -49.55) * mm, v(-78.1, -51.16) * mm, v(-77.22, -52.45) * mm, v(-76.28, -53.44) * mm]});
            skFitSpline(sketch, "E231", {"points": [v(-76.28, -53.44) * mm, v(-75.33, -54.42) * mm, v(-74.45, -54.98) * mm, v(-73.65, -55.13) * mm]});
            skFitSpline(sketch, "E232", {"points": [v(-73.65, -55.13) * mm, v(-72.85, -55.28) * mm, v(-72.45, -54.8) * mm, v(-72.45, -53.7) * mm, v(-72.45, -52.9) * mm, v(-71.88, -51.21) * mm, v(-70.75, -48.62) * mm, v(-69.62, -46.03) * mm, v(-68.13, -42.92) * mm, v(-66.27, -39.27) * mm]});
            skFitSpline(sketch, "E233", {"points": [v(-66.27, -39.27) * mm, v(-64.4, -35.62) * mm, v(-62.22, -31.6) * mm, v(-59.7, -27.18) * mm]});
            skFitSpline(sketch, "E234", {"points": [v(-59.7, -27.18) * mm, v(-57.19, -22.77) * mm, v(-54.55, -18.34) * mm, v(-51.77, -13.9) * mm]});
            skFitSpline(sketch, "E235", {"points": [v(-51.77, -13.9) * mm, v(-49, -9.44) * mm, v(-46.18, -5.12) * mm, v(-43.3, -0.93) * mm]});
            skFitSpline(sketch, "E236", {"points": [v(-43.3, -0.93) * mm, v(-40.42, 3.26) * mm, v(-37.65, 6.96) * mm, v(-34.98, 10.17) * mm]});
            skFitSpline(sketch, "E237", {"points": [v(-34.98, 10.17) * mm, v(-32.32, 13.38) * mm, v(-29.86, 15.97) * mm, v(-27.6, 17.94) * mm]});
            skFitSpline(sketch, "E238", {"points": [v(-27.6, 17.94) * mm, v(-25.34, 19.9) * mm, v(-23.44, 20.9) * mm, v(-21.9, 20.9) * mm, v(-20.75, 20.9) * mm, v(-19.98, 20.5) * mm, v(-19.61, 19.7) * mm]});
            skFitSpline(sketch, "E239", {"points": [v(-19.61, 19.7) * mm, v(-19.25, 18.89) * mm, v(-19.07, 18.09) * mm, v(-19.07, 17.28) * mm, v(-19.07, 16.4) * mm, v(-19.27, 15.31) * mm, v(-19.67, 14) * mm]});
            skFitSpline(sketch, "E240", {"points": [v(-19.67, 14) * mm, v(-20.07, 12.69) * mm, v(-20.62, 11.23) * mm, v(-21.3, 9.63) * mm]});
            skFitSpline(sketch, "E241", {"points": [v(-21.3, 9.63) * mm, v(-22, 8.02) * mm, v(-22.77, 6.33) * mm, v(-23.6, 4.54) * mm]});
            skFitSpline(sketch, "E242", {"points": [v(-23.6, 4.54) * mm, v(-24.45, 2.75) * mm, v(-25.3, 1.02) * mm, v(-26.18, -0.66) * mm]});
            skFitSpline(sketch, "E243", {"points": [v(-26.18, -0.66) * mm, v(-28.22, -4.67) * mm, v(-30.55, -8.93) * mm, v(-33.18, -13.45) * mm]});
            skFitSpline(sketch, "E244", {"points": [v(-33.18, -13.45) * mm, v(-36.46, -14.33) * mm, v(-39.38, -15.35) * mm, v(-41.93, -16.52) * mm]});
            skFitSpline(sketch, "E245", {"points": [v(-41.93, -16.52) * mm, v(-44.12, -17.54) * mm, v(-46.1, -18.74) * mm, v(-47.89, -20.13) * mm]});
            skFitSpline(sketch, "E246", {"points": [v(-47.89, -20.13) * mm, v(-49.68, -21.51) * mm, v(-50.57, -23.05) * mm, v(-50.57, -24.72) * mm, v(-50.57, -24.94) * mm, v(-50.53, -25.3) * mm, v(-50.46, -25.82) * mm]});
            skFitSpline(sketch, "E247", {"points": [v(-50.46, -25.82) * mm, v(-50.39, -26.33) * mm, v(-50.13, -26.85) * mm, v(-49.7, -27.4) * mm]});
            skFitSpline(sketch, "E248", {"points": [v(-49.7, -27.4) * mm, v(-49.26, -27.95) * mm, v(-48.59, -28.42) * mm, v(-47.67, -28.82) * mm]});
            skFitSpline(sketch, "E249", {"points": [v(-47.67, -28.82) * mm, v(-46.77, -29.23) * mm, v(-45.47, -29.42) * mm, v(-43.8, -29.42) * mm, v(-41.46, -29.42) * mm, v(-39.2, -29.04) * mm, v(-37.02, -28.28) * mm]});
            skFitSpline(sketch, "E250", {"points": [v(-37.02, -28.28) * mm, v(-34.84, -27.51) * mm, v(-32.72, -26.45) * mm, v(-30.68, -25.1) * mm]});
            skFitSpline(sketch, "E251", {"points": [v(-30.68, -25.1) * mm, v(-28.64, -23.76) * mm, v(-26.71, -22.17) * mm, v(-24.9, -20.35) * mm]});
            skFitSpline(sketch, "E252", {"points": [v(-24.9, -20.35) * mm, v(-23.07, -18.53) * mm, v(-21.32, -16.6) * mm, v(-19.65, -14.55) * mm, v(-19.64, -14.55) * mm, v(-19.64, -14.55) * mm, v(-19.1, -13.78) * mm, v(-19.1, -13.78) * mm, v(-19.1, -13.78) * mm, v(-16.33, -12.98) * mm, v(-13.49, -11.58) * mm, v(-10.57, -9.57) * mm]});
            skFitSpline(sketch, "E253", {"points": [v(-10.57, -9.57) * mm, v(-8.13, -7.9) * mm, v(-5.84, -6.14) * mm, v(-3.68, -4.3) * mm]});
            skFitSpline(sketch, "E254", {"points": [v(-3.68, -4.3) * mm, v(-3.77, -4.47) * mm, v(-3.88, -4.65) * mm, v(-3.97, -4.81) * mm]});
            skFitSpline(sketch, "E255", {"points": [v(-3.97, -4.81) * mm, v(-5.94, -8.31) * mm, v(-7.53, -11.4) * mm, v(-8.73, -14.06) * mm]});
            skFitSpline(sketch, "E256", {"points": [v(-8.73, -14.06) * mm, v(-9.93, -16.72) * mm, v(-10.53, -18.74) * mm, v(-10.53, -20.13) * mm, v(-10.53, -21.95) * mm, v(-10.04, -23.56) * mm, v(-9.06, -24.94) * mm]});
            skFitSpline(sketch, "E257", {"points": [v(-9.06, -24.94) * mm, v(-8.07, -26.33) * mm, v(-7.02, -27.4) * mm, v(-5.88, -28.17) * mm]});
            skFitSpline(sketch, "E258", {"points": [v(-5.88, -28.17) * mm, v(-4.76, -28.93) * mm, v(-3.7, -29.3) * mm, v(-2.71, -29.26) * mm]});
            skFitSpline(sketch, "E259", {"points": [v(-2.71, -29.26) * mm, v(-1.73, -29.23) * mm, v(-1.24, -28.66) * mm, v(-1.24, -27.57) * mm, v(-1.24, -26.25) * mm, v(-0.73, -24.65) * mm, v(0.3, -22.75) * mm]});
            skFitSpline(sketch, "E260", {"points": [v(0.3, -22.75) * mm, v(1.32, -20.86) * mm, v(2.68, -18.78) * mm, v(4.4, -16.52) * mm]});
            skFitSpline(sketch, "E261", {"points": [v(4.4, -16.52) * mm, v(6.11, -14.26) * mm, v(8.04, -11.9) * mm, v(10.2, -9.46) * mm]});
            skFitSpline(sketch, "E262", {"points": [v(10.2, -9.46) * mm, v(12.34, -7.02) * mm, v(14.55, -4.63) * mm, v(16.81, -2.3) * mm]});
            skFitSpline(sketch, "E263", {"points": [v(16.81, -2.3) * mm, v(22.14, 3.24) * mm, v(28.19, 9.12) * mm, v(34.97, 15.31) * mm]});
            skFitSpline(sketch, "E264", {"points": [v(34.97, 15.31) * mm, v(32.05, 10.94) * mm, v(29.43, 6.85) * mm, v(27.1, 3.06) * mm]});
            skFitSpline(sketch, "E265", {"points": [v(27.1, 3.06) * mm, v(26.07, 1.38) * mm, v(25.1, -0.27) * mm, v(24.2, -1.91) * mm]});
            skFitSpline(sketch, "E266", {"points": [v(24.2, -1.91) * mm, v(23.28, -3.55) * mm, v(22.45, -5.14) * mm, v(21.68, -6.67) * mm]});
            skFitSpline(sketch, "E267", {"points": [v(21.68, -6.67) * mm, v(20.92, -8.2) * mm, v(20.31, -9.59) * mm, v(19.88, -10.83) * mm]});
            skFitSpline(sketch, "E268", {"points": [v(19.88, -10.83) * mm, v(19.44, -12.07) * mm, v(19.22, -13.1) * mm, v(19.22, -13.9) * mm, v(19.22, -15.5) * mm, v(19.42, -17.21) * mm, v(19.82, -19.03) * mm]});
            skFitSpline(sketch, "E269", {"points": [v(19.82, -19.03) * mm, v(20.22, -20.86) * mm, v(20.82, -22.53) * mm, v(21.63, -24.07) * mm]});
            skFitSpline(sketch, "E270", {"points": [v(21.63, -24.07) * mm, v(22.43, -25.6) * mm, v(23.49, -26.87) * mm, v(24.8, -27.9) * mm]});
            skFitSpline(sketch, "E271", {"points": [v(24.8, -27.9) * mm, v(26.11, -28.92) * mm, v(27.64, -29.42) * mm, v(29.4, -29.42) * mm, v(31.07, -29.42) * mm, v(33.06, -28.62) * mm, v(35.35, -27.02) * mm]});
            skFitSpline(sketch, "E272", {"points": [v(35.35, -27.02) * mm, v(37.65, -25.42) * mm, v(40.08, -23.37) * mm, v(42.63, -20.9) * mm]});
            skFitSpline(sketch, "E273", {"points": [v(42.63, -20.9) * mm, v(44.45, -19.13) * mm, v(46.27, -17.23) * mm, v(48.09, -15.23) * mm]});
            skFitSpline(sketch, "E274", {"points": [v(48.09, -15.23) * mm, v(48.03, -15.7) * mm, v(47.99, -16.18) * mm, v(47.99, -16.63) * mm, v(47.99, -18.6) * mm, v(48.33, -20.36) * mm, v(49.03, -21.93) * mm]});
            skFitSpline(sketch, "E275", {"points": [v(49.03, -21.93) * mm, v(49.72, -23.5) * mm, v(50.6, -24.83) * mm, v(51.65, -25.93) * mm]});
            skFitSpline(sketch, "E276", {"points": [v(51.65, -25.93) * mm, v(52.7, -27.02) * mm, v(53.82, -27.88) * mm, v(54.99, -28.5) * mm]});
            skFitSpline(sketch, "E277", {"points": [v(54.99, -28.5) * mm, v(56.16, -29.12) * mm, v(57.25, -29.42) * mm, v(58.27, -29.42) * mm, v(59.3, -29.42) * mm, v(60.79, -28.59) * mm, v(62.76, -26.91) * mm]});
            skFitSpline(sketch, "E278", {"points": [v(62.76, -26.91) * mm, v(64.72, -25.23) * mm, v(66.7, -23.37) * mm, v(68.66, -21.33) * mm]});
            skFitSpline(sketch, "E279", {"points": [v(68.66, -21.33) * mm, v(71, -18.92) * mm, v(73.48, -16.23) * mm, v(76.1, -13.24) * mm]});
            skFitSpline(sketch, "E280", {"points": [v(76.1, -13.24) * mm, v(75.74, -14.04) * mm, v(75.4, -14.84) * mm, v(75.12, -15.64) * mm]});
            skFitSpline(sketch, "E281", {"points": [v(75.12, -15.64) * mm, v(74.9, -16.3) * mm, v(74.7, -17) * mm, v(74.51, -17.78) * mm]});
            skFitSpline(sketch, "E282", {"points": [v(74.51, -17.78) * mm, v(74.33, -18.54) * mm, v(74.24, -19.25) * mm, v(74.24, -19.9) * mm, v(74.24, -20.56) * mm, v(74.5, -21.44) * mm, v(75, -22.53) * mm]});
            skFitSpline(sketch, "E283", {"points": [v(75, -22.53) * mm, v(75.52, -23.63) * mm, v(76.17, -24.69) * mm, v(76.98, -25.7) * mm]});
            skFitSpline(sketch, "E284", {"points": [v(76.98, -25.7) * mm, v(77.78, -26.73) * mm, v(78.73, -27.6) * mm, v(79.82, -28.33) * mm]});
            skFitSpline(sketch, "E285", {"points": [v(79.82, -28.33) * mm, v(80.91, -29.06) * mm, v(82, -29.42) * mm, v(83.1, -29.42) * mm, v(84.78, -29.42) * mm, v(86.75, -28.64) * mm, v(89, -27.07) * mm]});
            skFitSpline(sketch, "E286", {"points": [v(89, -27.07) * mm, v(91.27, -25.5) * mm, v(93.64, -23.47) * mm, v(96.12, -21) * mm]});
            skFitSpline(sketch, "E287", {"points": [v(96.12, -21) * mm, v(98.6, -18.52) * mm, v(101.08, -15.8) * mm, v(103.56, -12.85) * mm]});
            skFitSpline(sketch, "E288", {"points": [v(103.56, -12.85) * mm, v(104.05, -12.26) * mm, v(104.53, -11.69) * mm, v(105, -11.11) * mm]});
            skFitSpline(sketch, "E289", {"points": [v(105, -11.11) * mm, v(104.7, -12.7) * mm, v(104.54, -14.28) * mm, v(104.54, -15.86) * mm, v(104.54, -19.29) * mm, v(105.09, -21.9) * mm, v(106.18, -23.68) * mm]});
            skFitSpline(sketch, "E290", {"points": [v(106.18, -23.68) * mm, v(107.28, -25.47) * mm, v(108.48, -26.8) * mm, v(109.8, -27.67) * mm]});
            skFitSpline(sketch, "E291", {"points": [v(109.8, -27.67) * mm, v(111.32, -28.7) * mm, v(113.07, -29.28) * mm, v(115.04, -29.42) * mm]});
            skFitSpline(sketch, "E292", {"points": [v(115.04, -29.42) * mm, v(117.37, -29.42) * mm, v(119.98, -28.62) * mm, v(122.86, -27.02) * mm]});
            skFitSpline(sketch, "E293", {"points": [v(122.86, -27.02) * mm, v(125.74, -25.42) * mm, v(128.7, -23.4) * mm, v(131.72, -20.95) * mm]});
            skFitSpline(sketch, "E294", {"points": [v(131.72, -20.95) * mm, v(134.75, -18.5) * mm, v(137.72, -15.8) * mm, v(140.64, -12.85) * mm]});
            skFitSpline(sketch, "E295", {"points": [v(140.64, -12.85) * mm, v(143.02, -10.44) * mm, v(145.22, -8.13) * mm, v(147.26, -5.92) * mm]});
            skFitSpline(sketch, "E296", {"points": [v(147.26, -5.92) * mm, v(146.7, -7.17) * mm, v(146.17, -8.39) * mm, v(145.73, -9.52) * mm]});
            skFitSpline(sketch, "E297", {"points": [v(145.73, -9.52) * mm, v(144.6, -12.36) * mm, v(144.03, -14.55) * mm, v(144.03, -16.08) * mm, v(144.03, -17.4) * mm, v(144.14, -18.83) * mm, v(144.36, -20.4) * mm]});
            skFitSpline(sketch, "E298", {"points": [v(144.36, -20.4) * mm, v(144.58, -21.97) * mm, v(145.03, -23.4) * mm, v(145.73, -24.72) * mm]});
            skFitSpline(sketch, "E299", {"points": [v(145.73, -24.72) * mm, v(146.42, -26.03) * mm, v(147.38, -27.15) * mm, v(148.62, -28.06) * mm]});
            skFitSpline(sketch, "E300", {"points": [v(148.62, -28.06) * mm, v(149.86, -28.97) * mm, v(151.5, -29.42) * mm, v(153.55, -29.42) * mm, v(155.22, -29.42) * mm, v(157.23, -28.6) * mm, v(159.56, -26.96) * mm]});
            skFitSpline(sketch, "E301", {"points": [v(159.56, -26.96) * mm, v(161.9, -25.32) * mm, v(164.36, -23.25) * mm, v(166.95, -20.73) * mm]});
            skFitSpline(sketch, "E302", {"points": [v(166.95, -20.73) * mm, v(169.53, -18.21) * mm, v(172.14, -15.44) * mm, v(174.77, -12.42) * mm]});
            skFitSpline(sketch, "E303", {"points": [v(174.77, -12.42) * mm, v(177.4, -9.4) * mm, v(179.8, -6.53) * mm, v(181.98, -3.83) * mm]});
            skFitSpline(sketch, "E304", {"points": [v(181.98, -3.83) * mm, v(184.16, -1.13) * mm, v(185.99, 1.24) * mm, v(187.47, 3.28) * mm]});
            skFitSpline(sketch, "E305", {"points": [v(187.47, 3.28) * mm, v(188.95, 5.32) * mm, v(189.87, 6.64) * mm, v(190.23, 7.22) * mm]});
            skFitSpline(sketch, "E306", {"points": [v(190.23, 7.22) * mm, v(190.8, 8.1) * mm, v(191.08, 8.82) * mm, v(191.04, 9.4) * mm]});
            skFitSpline(sketch, "E307", {"points": [v(191.04, 9.4) * mm, v(191, 10) * mm, v(190.8, 10.4) * mm, v(190.45, 10.61) * mm]});
            skFitSpline(sketch, "E308", {"points": [v(190.45, 10.61) * mm, v(190.09, 10.83) * mm, v(189.63, 10.85) * mm, v(189.1, 10.67) * mm]});
            skFitSpline(sketch, "E309", {"points": [v(189.1, 10.67) * mm, v(188.55, 10.48) * mm, v(188.1, 10.1) * mm, v(187.74, 9.52) * mm]});
            skFitSpline(sketch, "E310", {"points": [v(187.74, 9.52) * mm, v(185.36, 5.87) * mm, v(182.55, 2.1) * mm, v(179.3, -1.8) * mm]});
            skFitSpline(sketch, "E311", {"points": [v(179.3, -1.8) * mm, v(176.06, -5.7) * mm, v(172.9, -9.28) * mm, v(169.84, -12.53) * mm]});
            skFitSpline(sketch, "E312", {"points": [v(169.84, -12.53) * mm, v(166.78, -15.77) * mm, v(164.05, -18.45) * mm, v(161.64, -20.56) * mm]});
            skFitSpline(sketch, "E313", {"points": [v(161.64, -20.56) * mm, v(159.23, -22.68) * mm, v(157.63, -23.74) * mm, v(156.83, -23.74) * mm, v(155.51, -23.74) * mm, v(155.02, -22.77) * mm, v(155.35, -20.84) * mm]});
            skFitSpline(sketch, "E314", {"points": [v(155.35, -20.84) * mm, v(155.68, -18.9) * mm, v(156.59, -16.32) * mm, v(158.08, -13.07) * mm]});
            skFitSpline(sketch, "E315", {"points": [v(-39.13, -21.88) * mm, v(-39.7, -22.46) * mm, v(-40.27, -23) * mm, v(-40.81, -23.52) * mm]});
            skFitSpline(sketch, "E316", {"points": [v(-40.81, -23.52) * mm, v(-41.35, -24.03) * mm, v(-41.84, -24.4) * mm, v(-42.27, -24.61) * mm]});
            skFitSpline(sketch, "E317", {"points": [v(-42.27, -24.61) * mm, v(-42.7, -24.83) * mm, v(-43.05, -24.85) * mm, v(-43.3, -24.67) * mm]});
            skFitSpline(sketch, "E318", {"points": [v(-43.3, -24.67) * mm, v(-43.55, -24.48) * mm, v(-43.68, -24.07) * mm, v(-43.68, -23.4) * mm]});
            skFitSpline(sketch, "E319", {"points": [v(-43.68, -23.4) * mm, v(-43.68, -22.68) * mm, v(-43.21, -21.91) * mm, v(-42.27, -21.11) * mm]});
            skFitSpline(sketch, "E320", {"points": [v(-42.27, -21.11) * mm, v(-41.33, -20.31) * mm, v(-40.29, -19.54) * mm, v(-39.13, -18.81) * mm]});
            skFitSpline(sketch, "E321", {"points": [v(-39.13, -18.81) * mm, v(-37.83, -18.01) * mm, v(-36.32, -17.21) * mm, v(-34.59, -16.4) * mm]});
            skFitSpline(sketch, "E322", {"points": [v(-34.59, -16.4) * mm, v(-36.32, -18.67) * mm, v(-37.83, -20.5) * mm, v(-39.13, -21.88) * mm]});
            skFitSpline(sketch, "E323", {"points": [v(126.3, 0.1) * mm, v(127.33, 1.5) * mm, v(128.37, 2.88) * mm, v(129.43, 4.27) * mm]});
            skFitSpline(sketch, "E324", {"points": [v(129.43, 4.27) * mm, v(130.48, 5.65) * mm, v(131.47, 6.9) * mm, v(132.38, 7.99) * mm]});
            skFitSpline(sketch, "E325", {"points": [v(132.38, 7.99) * mm, v(133.3, 9.08) * mm, v(134.15, 9.95) * mm, v(134.95, 10.61) * mm]});
            skFitSpline(sketch, "E326", {"points": [v(134.95, 10.61) * mm, v(135.75, 11.27) * mm, v(136.37, 11.6) * mm, v(136.81, 11.6) * mm, v(137.25, 11.6) * mm, v(137.53, 11.4) * mm, v(137.66, 11) * mm]});
            skFitSpline(sketch, "E327", {"points": [v(137.66, 11) * mm, v(137.79, 10.62) * mm, v(137.76, 10.03) * mm, v(137.58, 9.24) * mm]});
            skFitSpline(sketch, "E328", {"points": [v(137.58, 9.24) * mm, v(137.2, 7.67) * mm, v(136.23, 5.72) * mm, v(134.62, 3.4) * mm]});
            skFitSpline(sketch, "E329", {"points": [v(134.62, 3.4) * mm, v(133.02, 1.06) * mm, v(130.87, -1.44) * mm, v(128.17, -4.1) * mm]});
            skFitSpline(sketch, "E330", {"points": [v(128.17, -4.1) * mm, v(125.47, -6.77) * mm, v(122.26, -9.19) * mm, v(118.54, -11.38) * mm]});
            skFitSpline(sketch, "E331", {"points": [v(118.54, -11.38) * mm, v(121.31, -7.15) * mm, v(123.9, -3.32) * mm, v(126.3, 0.1) * mm]});
            skSolve(sketch);
        }
        {
            var Q0;
            Q0 = qSketchRegion(id + "F0", true);
            extrude(context, id + "F1", {"entities" : qUnion([Q0]), "domain" : OperationDomain.MODEL, "flatOperationType" : FlatOperationType.REMOVE, "depth" : 30 * mm, "offsetDistance" : 25 * mm});
        }
    });
